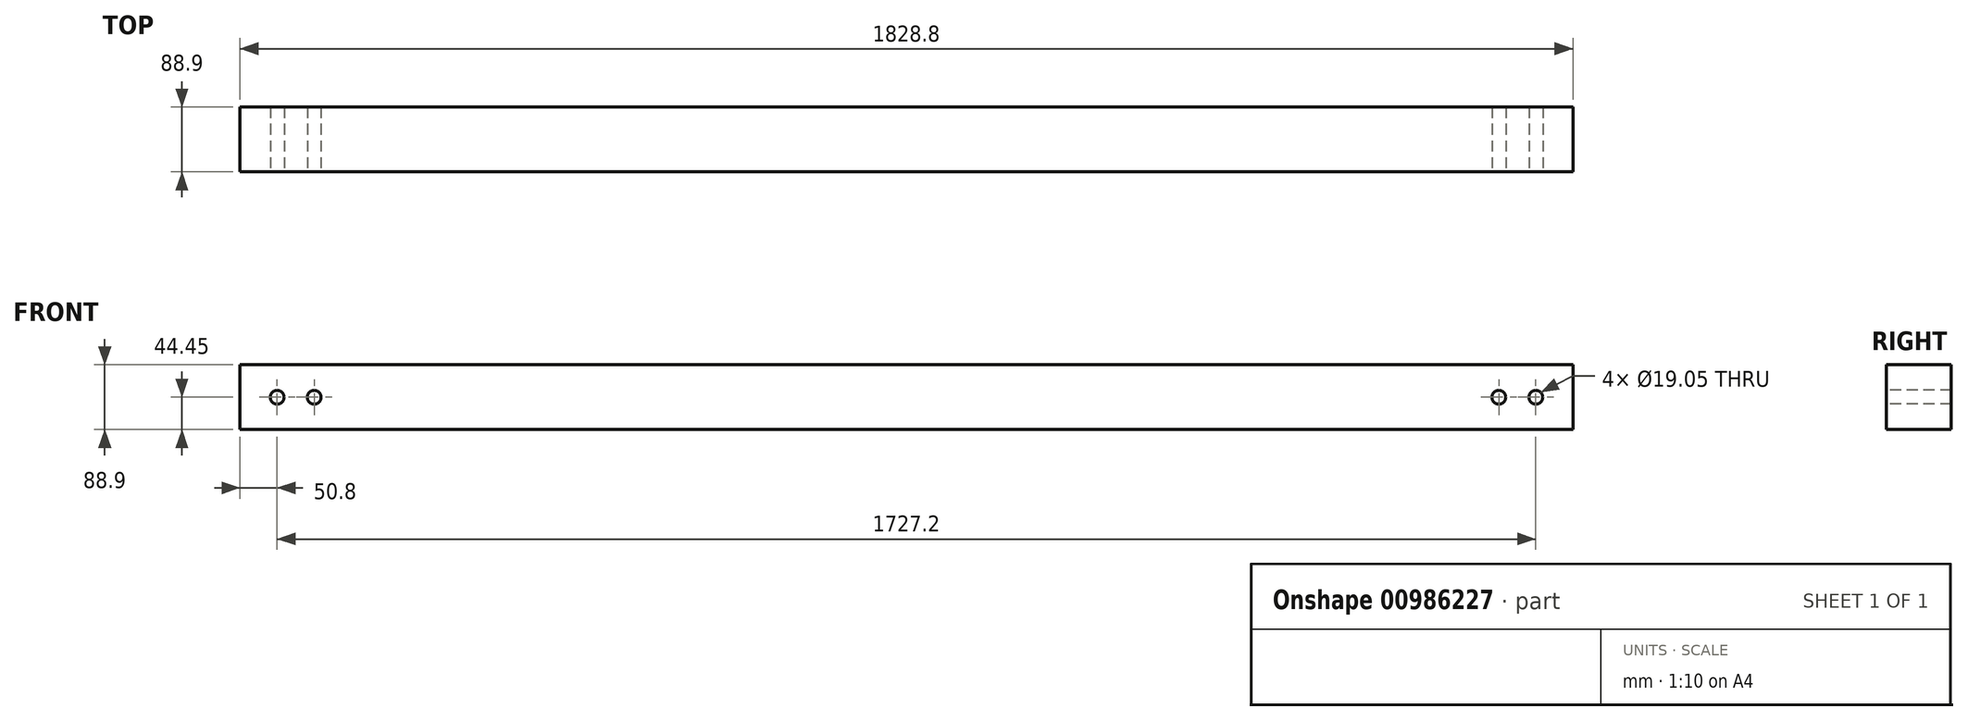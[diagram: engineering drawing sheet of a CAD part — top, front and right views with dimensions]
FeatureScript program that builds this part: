
annotation { "Feature Type Name" : "Feature", "Feature Type Description" : "" }
export const myFeature = defineFeature(function(context is Context, id is Id, definition is map)
    precondition{}
    {
        {
            var Q0;
            Q0=qCreatedBy(makeId("Right.planeOp"),FACE);
            var sketch = newSketch(context, id + "F0", { "sketchPlane" : qUnion([Q0])});
            skLineSegment(sketch, "E0.bottom", {"start": v(-44.45, 44.45) * mm, "end": v(44.45, 44.45) * mm});
            skLineSegment(sketch, "E0.top", {"start": v(-44.45, -44.45) * mm, "end": v(44.45, -44.45) * mm});
            skLineSegment(sketch, "E0.left", {"start": v(-44.45, 44.45) * mm, "end": v(-44.45, -44.45) * mm});
            skLineSegment(sketch, "E0.right", {"start": v(44.45, 44.45) * mm, "end": v(44.45, -44.45) * mm});
            skPoint(sketch, "E0.middle", {"position": v(0, 0) * mm});
            skSolve(sketch);
        }
        {
            var Q0;
            Q0=makeQuery(id+"F0.imprint","IMPRINT",FACE,{"disambiguationData":[TD([[makeQuery(id+"F0.imprint","IMPRINT",EDGE,{"derivedFrom":sQuery(id+"F0.wireOp",EDGE,"E0.bottom")}),-1.0]])]});
            extrude(context, id + "F1", {"entities" : qUnion([Q0]), "depth" : 1828.8 * mm, "offsetDistance" : 25.4 * mm});
        }
        {
            var Q0;
            Q0=makeQuery(id+"F1.opExtrude","SWEPT_FACE",FACE,{"disambiguationData":[OSD([sQuery(id+"F0.wireOp",EDGE,"E0.left")])]});
            var sketch = newSketch(context, id + "F2", { "sketchPlane" : qUnion([Q0])});
            skCircle(sketch, "E1", {"center": v(1778, 0) * mm, "radius": 9.53 * mm});
            skCircle(sketch, "E2", {"center": v(1727.2, 0) * mm, "radius": 9.53 * mm});
            skCircle(sketch, "E3.1.0.0", {"center": v(101.6, 0) * mm, "radius": 9.53 * mm});
            skCircle(sketch, "E3.1.0.1", {"center": v(50.8, 0) * mm, "radius": 9.53 * mm});
            skLineSegment(sketch, "E3.direction1", {"start": v(1778, 0) * mm, "end": v(101.6, 0) * mm, "construction": true});
            skSolve(sketch);
        }
        {
            var Q0;
            Q0=sQuery(id+"F2.wireOp",VERTEX,"E3.1.0.1.center");
            var Q1;
            Q1=sQuery(id+"F2.wireOp",VERTEX,"E3.direction1.end");
            var Q2;
            Q2=sQuery(id+"F2.wireOp",VERTEX,"E3.direction1.start");
            var Q3;
            Q3=sQuery(id+"F2.wireOp",VERTEX,"E2.center");
            var Q4;
            Q4=makeQuery(id+"F1.opExtrude","SWEPT_BODY",BODY,{"disambiguationData":[OSD([sQuery(id+"F0.wireOp",EDGE,"E0.bottom"),sQuery(id+"F0.wireOp",EDGE,"E0.top"),sQuery(id+"F0.wireOp",EDGE,"E0.left"),sQuery(id+"F0.wireOp",EDGE,"E0.right")])]});
            hole(context, id + "F3", {"style" : HoleStyle.C_BORE, "endStyle" : HoleEndStyle.THROUGH, "holeDiameter" : 19.05 * mm, "cBoreDiameter" : 19.05 * mm, "cBoreDepth" : 19.05 * mm, "majorDiameter" : 6.35 * mm, "isTappedThrough" : true, "tappedDepth" : 12.7 * mm, "tapClearance" : 3, "locations" : qUnion([Q0, Q1, Q2, Q3]), "scope" : qUnion([Q4])});
        }
    });
